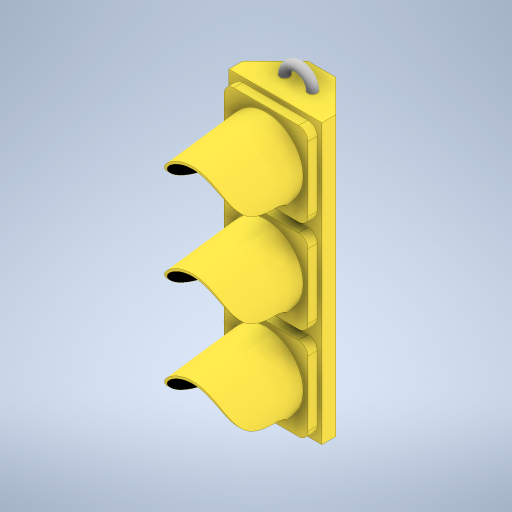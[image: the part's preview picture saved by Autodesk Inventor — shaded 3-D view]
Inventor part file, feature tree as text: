
AUTODESK INVENTOR PART (.ipt)
format: ipt  version: 2024 (Build 280153000, 153)  size: 534,528 bytes
history: native  units: in
note: dims shown in document units (in); Inventor stores cm internally (conversion verified against a paired STEP export)
features: sketch x11, extrude x4, sweep x3, projected_geometry x3, revolve x2
ambient origin geometry x8: Origin, YZ Plane, XZ Plane, XY Plane, X Axis, Y Axis, Z Axis, Center Point
bodies: Solid1 (feature_tree)
feature tree (23):
  extrude  "Extrusion1"  Depth=30.0in
  sketch  "Sketch2"  dims[d2=10.0in d3=6.0in d4=0.0in]
  sketch  "Sketch3"  dims[d11=1.0in d12=1.0in]
  sketch  "Sketch5"  dims[d19=8.0in d20=7.5in]
  sketch  "Sketch4"  dims[d17=8.0in d18=7.5in]
  sweep  "Sweep1"
  sweep  "Sweep2"
  sweep  "Sweep3"
  extrude  "Extrusion2"  Depth=7.5in
  extrude  "Extrusion3"  Depth=7.5in
  extrude  "Extrusion4"  Depth=0.055in
  sketch  "Sketch9"  dims[d27=8.0in d28=0.055in]
  revolve  "Revolution1"  [1 undecoded]
  sketch  "Sketch11"  dims[d29=0.0in d30=0.0in]
  sketch  "Sketch12"  dims[d31=0.0in d32=0.0in d33=0.0in d34=0.0in d38=4.0in d39=30.5625in d40=0.0in d41=9.0in d42=9.0in d43=9.0in d44=9.0in d45=1.0in d46=1.0in d47=0.0in d49=45.0deg d50=135.0deg d51=30.875in d52=0.0in d53=1.0in d54=1.0in d57=180.0deg d58=0.5in d59=0.5in d60=0.5in d61=0.5in d62=0.5in d63=0.5in d64=180.0deg]
  revolve  "Revolution2"  [1 undecoded]
  sketch  "Sketch1"  dims[d0=11.5in d1=30.0in]
  sketch  "Sketch6"  dims[d21=8.0in d22=7.5in]
  sketch  "Sketch7"  dims[d23=8.0in d24=0.055in]
  sketch  "Sketch8"  dims[d25=8.0in d26=0.055in]
  projected_geometry  "Project Cut Edges1"
  projected_geometry  "Project Cut Edges2"
  projected_geometry  "Project Cut Edges3"
note: 2 required parameter values undecoded (feature->parameter linkage not recoverable at this tier; creation-order binding heuristic only, values carry confidence <= 0.55)
